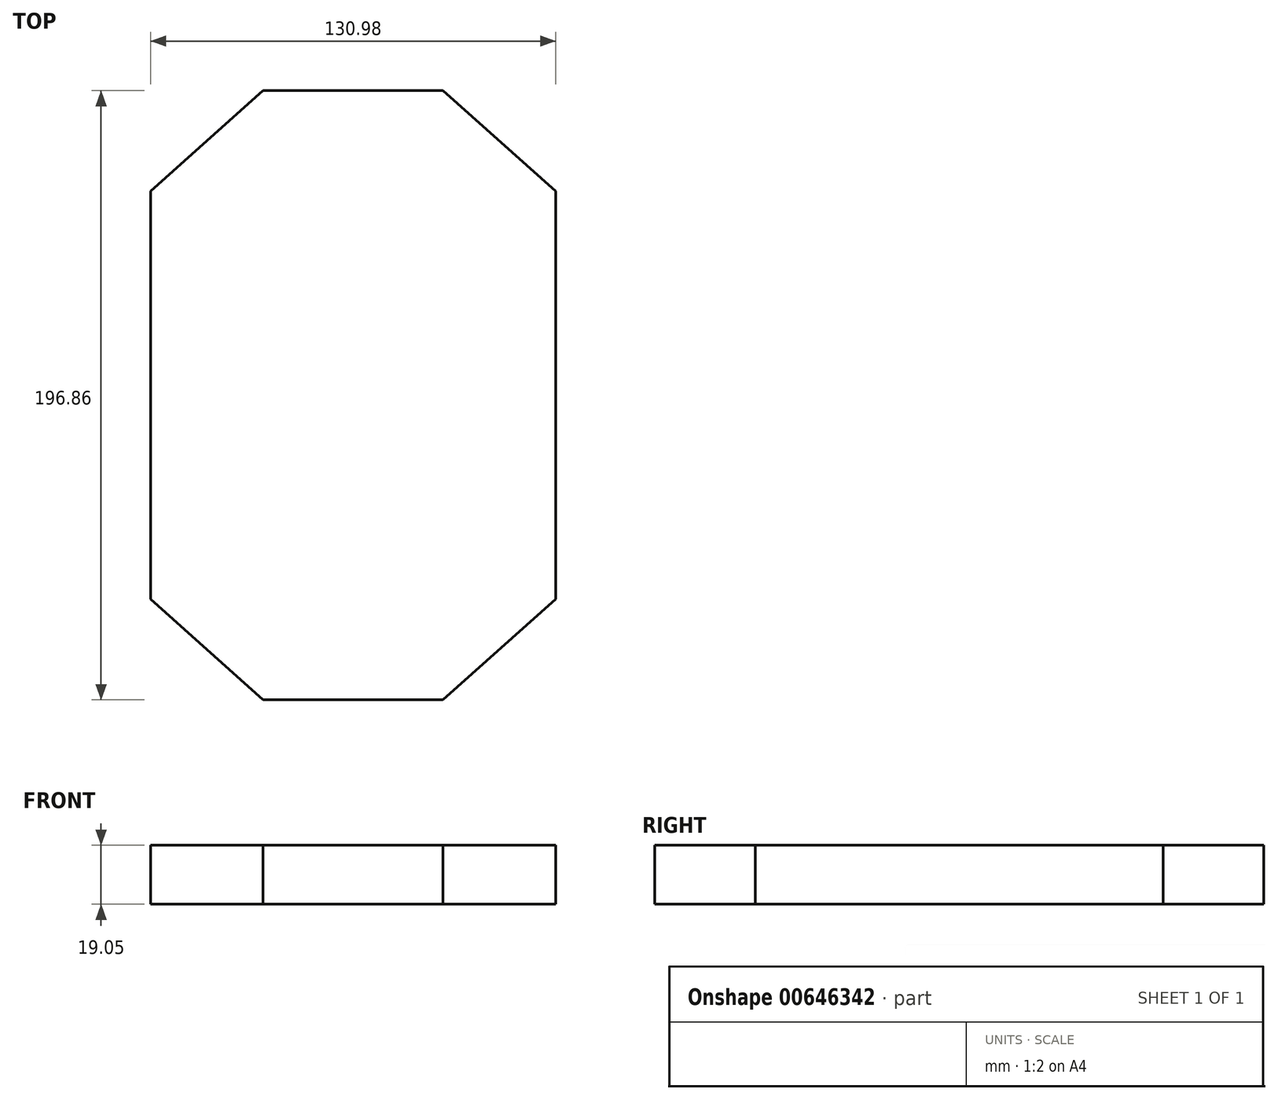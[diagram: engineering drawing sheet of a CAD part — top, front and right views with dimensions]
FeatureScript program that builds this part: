
annotation { "Feature Type Name" : "Feature", "Feature Type Description" : "" }
export const myFeature = defineFeature(function(context is Context, id is Id, definition is map)
    precondition{}
    {
        {
            var Q0;
            Q0=qCreatedBy(makeId("Top.planeOp"),FACE);
            var sketch = newSketch(context, id + "F0", { "sketchPlane" : qUnion([Q0])});
            skLineSegment(sketch, "E0.bottom", {"start": v(29.08, 98.43) * mm, "end": v(-29.08, 98.43) * mm});
            skLineSegment(sketch, "E0.top", {"start": v(29.08, -98.43) * mm, "end": v(-29.08, -98.43) * mm});
            skLineSegment(sketch, "E0.left", {"start": v(29.08, 98.43) * mm, "end": v(29.08, -98.43) * mm});
            skLineSegment(sketch, "E0.right", {"start": v(-29.08, 98.43) * mm, "end": v(-29.08, -98.43) * mm});
            skPoint(sketch, "E0.middle", {"position": v(0, 0) * mm});
            skLineSegment(sketch, "E1.bottom", {"start": v(-65.49, 65.91) * mm, "end": v(65.49, 65.91) * mm});
            skLineSegment(sketch, "E1.top", {"start": v(-65.49, -65.91) * mm, "end": v(65.49, -65.91) * mm});
            skLineSegment(sketch, "E1.left", {"start": v(-65.49, 65.91) * mm, "end": v(-65.49, -65.91) * mm});
            skLineSegment(sketch, "E1.right", {"start": v(65.49, 65.91) * mm, "end": v(65.49, -65.91) * mm});
            skLineSegment(sketch, "E2", {"start": v(-29.08, -98.43) * mm, "end": v(-65.49, -65.91) * mm});
            skLineSegment(sketch, "E3", {"start": v(29.08, -98.43) * mm, "end": v(65.49, -65.91) * mm});
            skLineSegment(sketch, "E4", {"start": v(65.49, 65.91) * mm, "end": v(29.08, 98.43) * mm});
            skLineSegment(sketch, "E5", {"start": v(-65.49, 65.91) * mm, "end": v(-29.08, 98.43) * mm});
            skSolve(sketch);
        }
        {
            var Q0;
            {var subQ0=sQuery(id+"F0.wireOp",EDGE,"E0.bottom");Q0=makeQuery(id+"F0.imprint","IMPRINT",FACE,{"disambiguationData":[TD([[makeQuery(id+"F0.imprint","IMPRINT",EDGE,{"derivedFrom":subQ0}),1.0]])]});}
            var Q1;
            {var subQ5=sQuery(id+"F0.wireOp",EDGE,"E1.left");Q1=makeQuery(id+"F0.imprint","IMPRINT",FACE,{"disambiguationData":[TD([[makeQuery(id+"F0.imprint","IMPRINT",EDGE,{"derivedFrom":subQ5}),1.0]])]});}
            var Q2;
            {var subQ0=sQuery(id+"F0.wireOp",EDGE,"E5");Q2=makeQuery(id+"F0.imprint","IMPRINT",FACE,{"disambiguationData":[TD([[makeQuery(id+"F0.imprint","IMPRINT",EDGE,{"derivedFrom":subQ0}),-1.0]])]});}
            var Q3;
            {var subQ0=sQuery(id+"F0.wireOp",EDGE,"E1.bottom");var subQ1=sQuery(id+"F0.wireOp",EDGE,"E0.left");var subQ2=makeQuery(id+"F0.imprint","INTERSECT",VERTEX,{"derivedFrom":[subQ1,subQ0]});Q3=makeQuery(id+"F0.imprint","IMPRINT",FACE,{"disambiguationData":[TD([[makeQuery(id+"F0.imprint","IMPRINT",EDGE,{"disambiguationData":[TD([[subQ2,-1.0]])],"derivedFrom":subQ1}),-1.0]])]});}
            var Q4;
            {var subQ5=sQuery(id+"F0.wireOp",EDGE,"E1.right");Q4=makeQuery(id+"F0.imprint","IMPRINT",FACE,{"disambiguationData":[TD([[makeQuery(id+"F0.imprint","IMPRINT",EDGE,{"derivedFrom":subQ5}),-1.0]])]});}
            var Q5;
            {var subQ0=sQuery(id+"F0.wireOp",EDGE,"E4");Q5=makeQuery(id+"F0.imprint","IMPRINT",FACE,{"disambiguationData":[TD([[makeQuery(id+"F0.imprint","IMPRINT",EDGE,{"derivedFrom":subQ0}),1.0]])]});}
            var Q6;
            {var subQ0=sQuery(id+"F0.wireOp",EDGE,"E3");Q6=makeQuery(id+"F0.imprint","IMPRINT",FACE,{"disambiguationData":[TD([[makeQuery(id+"F0.imprint","IMPRINT",EDGE,{"derivedFrom":subQ0}),1.0]])]});}
            var Q7;
            {var subQ0=sQuery(id+"F0.wireOp",EDGE,"E0.top");Q7=makeQuery(id+"F0.imprint","IMPRINT",FACE,{"disambiguationData":[TD([[makeQuery(id+"F0.imprint","IMPRINT",EDGE,{"derivedFrom":subQ0}),-1.0]])]});}
            var Q8;
            {var subQ0=sQuery(id+"F0.wireOp",EDGE,"E2");Q8=makeQuery(id+"F0.imprint","IMPRINT",FACE,{"disambiguationData":[TD([[makeQuery(id+"F0.imprint","IMPRINT",EDGE,{"derivedFrom":subQ0}),-1.0]])]});}
            extrude(context, id + "F1", {"entities" : qUnion([Q0, Q1, Q2, Q3, Q4, Q5, Q6, Q7, Q8]), "depth" : 19.05 * mm, "offsetDistance" : 25.4 * mm});
        }
    });
